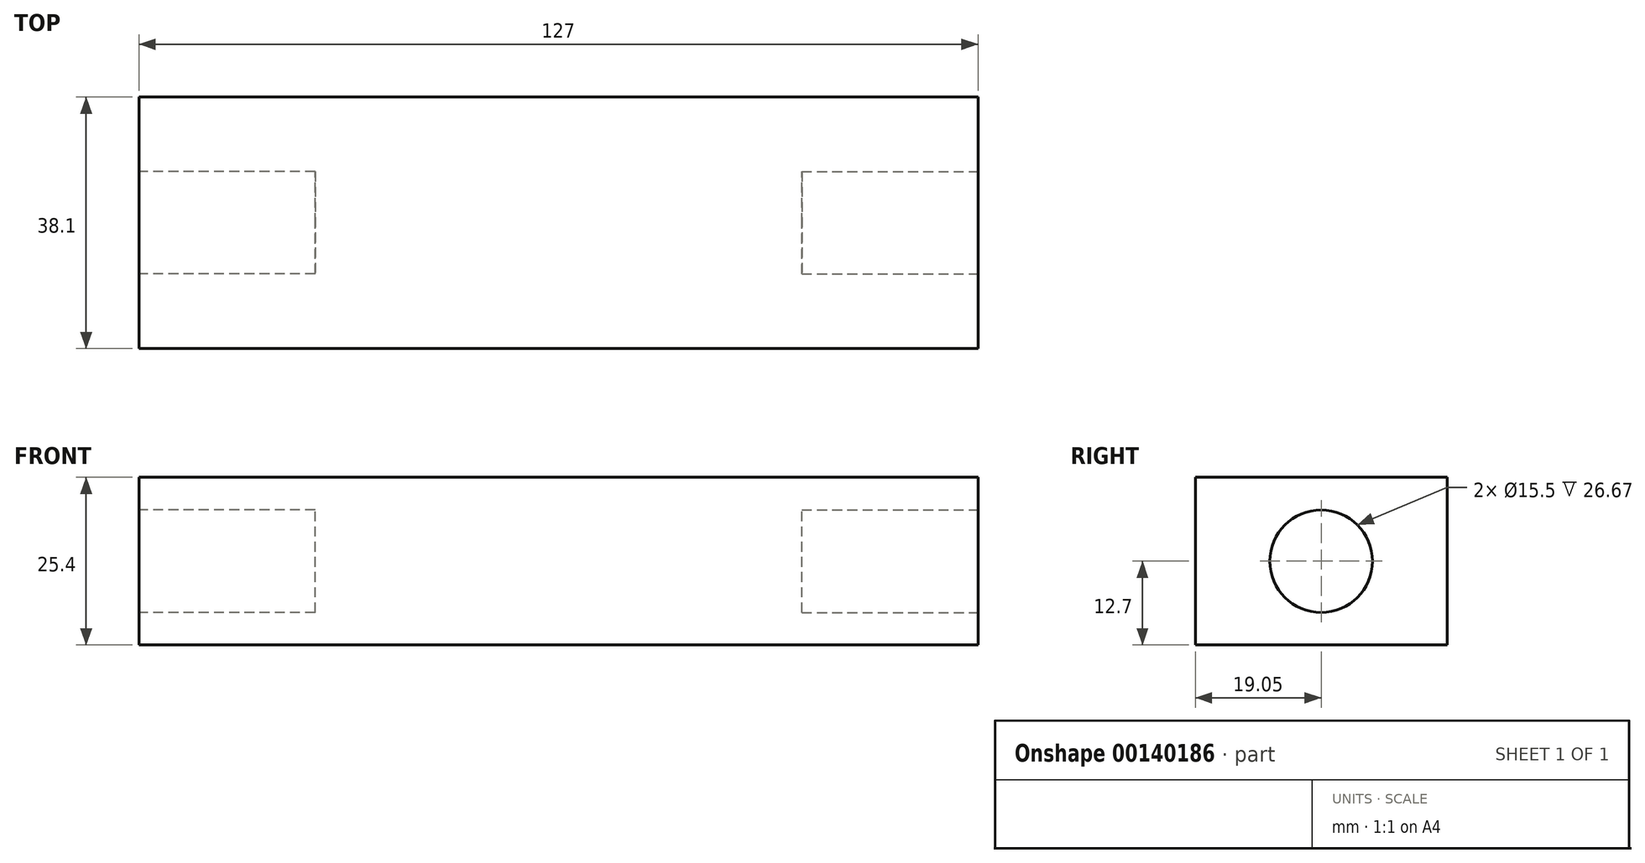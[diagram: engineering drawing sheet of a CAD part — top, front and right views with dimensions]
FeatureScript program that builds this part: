
annotation { "Feature Type Name" : "Feature", "Feature Type Description" : "" }
export const myFeature = defineFeature(function(context is Context, id is Id, definition is map)
    precondition{}
    {
        {
            var Q0;
            Q0=qCreatedBy(makeId("Right.planeOp"),FACE);
            var sketch = newSketch(context, id + "F0", { "sketchPlane" : qUnion([Q0])});
            skLineSegment(sketch, "E0.bottom", {"start": v(0, 25.4) * mm, "end": v(-38.1, 25.4) * mm});
            skLineSegment(sketch, "E0.top", {"start": v(0, 0) * mm, "end": v(-38.1, 0) * mm});
            skLineSegment(sketch, "E0.left", {"start": v(0, 25.4) * mm, "end": v(0, 0) * mm});
            skLineSegment(sketch, "E0.right", {"start": v(-38.1, 25.4) * mm, "end": v(-38.1, 0) * mm});
            skPoint(sketch, "E0.middle", {"position": v(0, 0) * mm});
            skSolve(sketch);
        }
        {
            var Q0;
            Q0=qSketchRegion(id+"F0",true);
            extrude(context, id + "F1", {"entities" : qUnion([Q0]), "depth" : 63.5 * mm});
        }
        {
            var Q0;
            Q0=makeQuery(id+"F1.opExtrude","CAP_FACE",FACE,{"disambiguationData":[OSD([sQuery(id+"F0.wireOp",EDGE,"E0.bottom"),sQuery(id+"F0.wireOp",EDGE,"E0.top"),sQuery(id+"F0.wireOp",EDGE,"E0.left"),sQuery(id+"F0.wireOp",EDGE,"E0.right")])],"isStart":false});
            var sketch = newSketch(context, id + "F2", { "sketchPlane" : qUnion([Q0])});
            skCircle(sketch, "E1", {"center": v(-19.05, 12.7) * mm, "radius": 7.75 * mm});
            skLineSegment(sketch, "E2", {"start": v(-19.05, 0) * mm, "end": v(-19.05, 12.7) * mm, "construction": true});
            skSolve(sketch);
        }
        {
            var Q0;
            Q0=qSketchRegion(id+"F2",true);
            extrude(context, id + "F3", {"entities" : qUnion([Q0]), "operationType" : NewBodyOperationType.REMOVE, "oppositeDirection" : true, "depth" : 26.67 * mm});
        }
        {
            var Q0;
            Q0=makeQuery(id+"F1.opExtrude","SWEPT_BODY",BODY,{"disambiguationData":[OSD([sQuery(id+"F0.wireOp",EDGE,"E0.bottom"),sQuery(id+"F0.wireOp",EDGE,"E0.top"),sQuery(id+"F0.wireOp",EDGE,"E0.left"),sQuery(id+"F0.wireOp",EDGE,"E0.right")])]});
            var Q1;
            Q1=qCreatedBy(makeId("Right.planeOp"),FACE);
            mirror(context, id + "F4", {"operationType" : NewBodyOperationType.ADD, "entities" : qUnion([Q0]), "mirrorPlane" : qUnion([Q1])});
        }
    });
